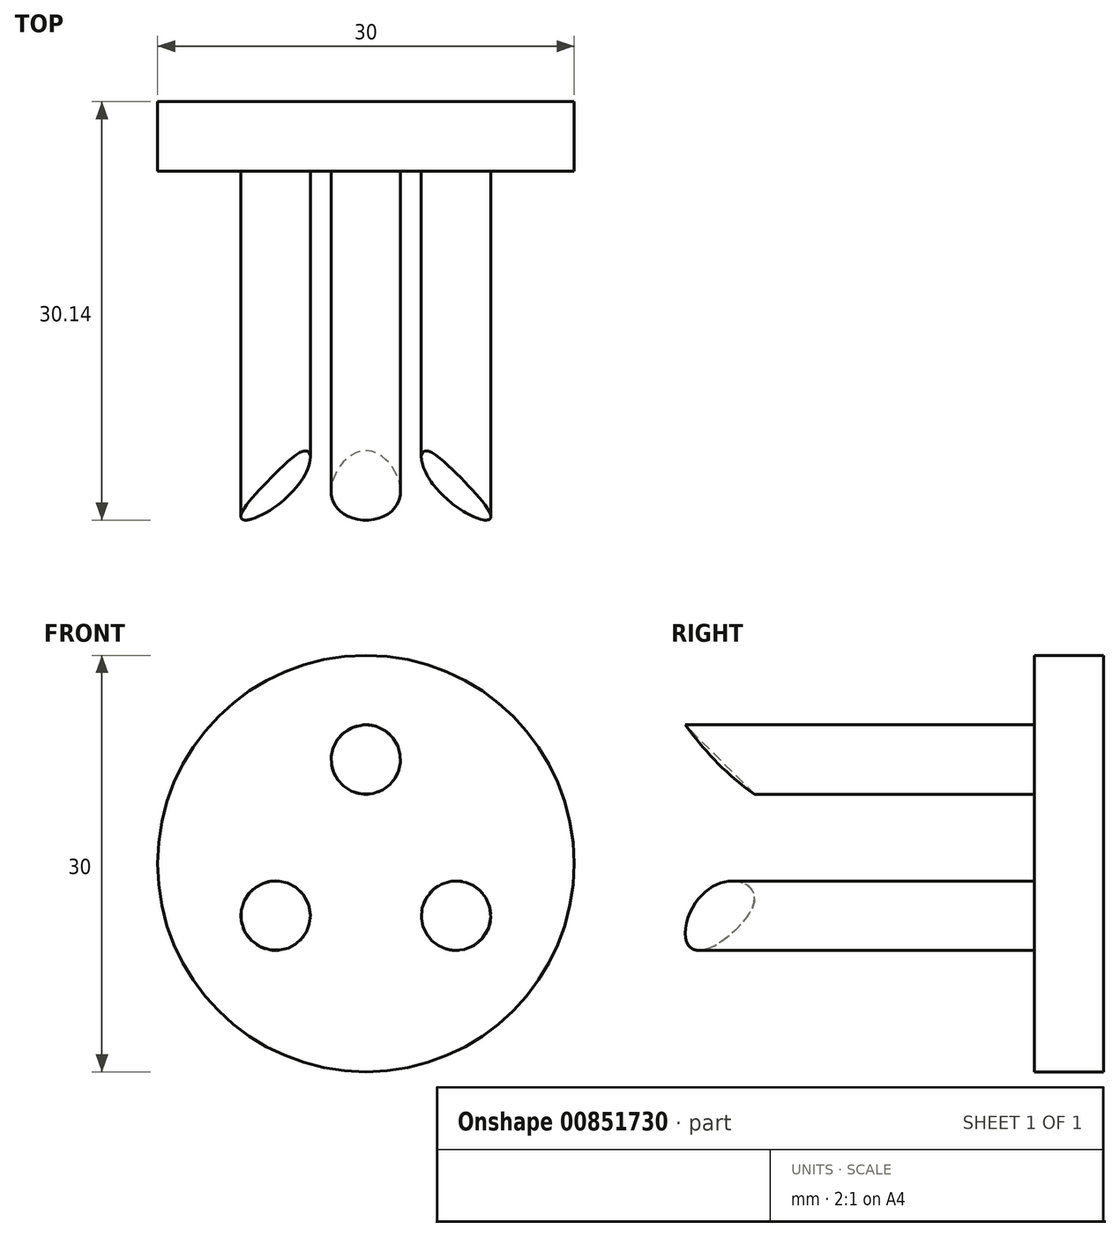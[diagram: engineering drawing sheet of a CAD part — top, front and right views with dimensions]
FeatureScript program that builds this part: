
annotation { "Feature Type Name" : "Feature", "Feature Type Description" : "" }
export const myFeature = defineFeature(function(context is Context, id is Id, definition is map)
    precondition{}
    {
        {
            var Q0;
            Q0=qCreatedBy(makeId("Front.planeOp"),FACE);
            var sketch = newSketch(context, id + "F0", { "sketchPlane" : qUnion([Q0])});
            skCircle(sketch, "E0", {"center": v(0, 0) * mm, "radius": 15 * mm});
            skSolve(sketch);
        }
        {
            var Q0;
            Q0 = qSketchRegion(id + "F0", true);
            extrude(context, id + "F1", {"entities" : qUnion([Q0]), "depth" : 5 * mm, "offsetDistance" : 25.4 * mm});
        }
        {
            var Q0;
            Q0=makeQuery(id+"F1.opExtrude","CAP_FACE",FACE,{"disambiguationData":[OSD([sQuery(id+"F0.wireOp",EDGE,"E0")])],"isStart":false});
            var sketch = newSketch(context, id + "F2", { "sketchPlane" : qUnion([Q0])});
            skCircle(sketch, "E1", {"center": v(0, 7.5) * mm, "radius": 2.5 * mm});
            skLineSegment(sketch, "E2", {"start": v(0, 0) * mm, "end": v(0, 15) * mm, "construction": true});
            skLineSegment(sketch, "E3", {"start": v(0, 0) * mm, "end": v(13, -7.5) * mm, "construction": true});
            skLineSegment(sketch, "E4", {"start": v(0, 0) * mm, "end": v(-13, -7.5) * mm, "construction": true});
            skCircle(sketch, "E5", {"center": v(-6.5, -3.75) * mm, "radius": 2.5 * mm});
            skCircle(sketch, "E6", {"center": v(6.5, -3.75) * mm, "radius": 2.5 * mm});
            skSolve(sketch);
        }
        {
            var Q0;
            Q0=makeQuery(id+"F2.imprint","IMPRINT",FACE,{"disambiguationData":[TD([[makeQuery(id+"F2.imprint","IMPRINT",EDGE,{"derivedFrom":sQuery(id+"F2.wireOp",EDGE,"E5")}),1.0]])]});
            var Q1;
            Q1=makeQuery(id+"F2.imprint","IMPRINT",FACE,{"disambiguationData":[TD([[makeQuery(id+"F2.imprint","IMPRINT",EDGE,{"derivedFrom":sQuery(id+"F2.wireOp",EDGE,"E1")}),1.0]])]});
            var Q2;
            Q2=makeQuery(id+"F2.imprint","IMPRINT",FACE,{"disambiguationData":[TD([[makeQuery(id+"F2.imprint","IMPRINT",EDGE,{"derivedFrom":sQuery(id+"F2.wireOp",EDGE,"E6")}),1.0]])]});
            extrude(context, id + "F3", {"entities" : qUnion([Q0, Q1, Q2]), "operationType" : NewBodyOperationType.ADD, "depth" : 25.4 * mm, "offsetDistance" : 25.4 * mm});
        }
        {
            var Q0;
            Q0=qCreatedBy(makeId("Right.planeOp"),FACE);
            var sketch = newSketch(context, id + "F4", { "sketchPlane" : qUnion([Q0])});
            skLineSegment(sketch, "E7", {"start": v(-30.42, 10.27) * mm, "end": v(-30.42, 0) * mm});
            skLineSegment(sketch, "E8", {"start": v(-30.42, 0) * mm, "end": v(-20.14, 0) * mm});
            skLineSegment(sketch, "E9", {"start": v(-20.14, 0) * mm, "end": v(-30.42, 10.27) * mm});
            skLineSegment(sketch, "E10", {"start": v(0, 0) * mm, "end": v(-43.26, 0) * mm, "construction": true});
            skSolve(sketch);
        }
        {
            var Q0;
            Q0 = qSketchRegion(id + "F4", true);
            var Q1;
            Q1=sQuery(id+"F4.wireOp",EDGE,"E10");
            revolve(context, id + "F5", {"operationType" : NewBodyOperationType.REMOVE, "surfaceOperationType" : NewSurfaceOperationType.NEW, "entities" : qUnion([Q0]), "axis" : qUnion([Q1]), "revolveType" : RevolveType.FULL});
        }
    });
